# Revit family: QF_TRUE_TCGG-48-LD
name_source: partatom
category: Specialty Equipment
revit_build: Autodesk Revit 2014 (Build: 20130308_1515(x64)
units: mm (PartAtom-declared; Revit-internal decimal feet)

## types (1)
- DefaultType
    Apparent Power = 1357 VA
    Conn Conduit = Yes
    Conn Plug = 5-15P
    Cycle = 60 Hz
    Description = DISPLAY CASE: CURVED GLASS REFRIGERATED DELI CASE WITH LED LIGHTING
    FL Amps = 12 A
    HP = 1/3
    KCL SpecSheet URL = http://kclweb.kclcad.com
    KCLRef = KCL2C9,,0004091d-0000-0000-0000-000000000307,TF,TCGG-48 ,634854572620000000,716ea76f-1d88-4e94-8cc5-f22e7c59b278,a3fedd8f-e5fe-44fd-9469-5db82f1f6102
    Manufacturer = TRUE FOOD SERVICE EQUIPMENT, INC.
    Max Overcurrent Protection = 17 A
    Min Ckt Ampacity = 12 A
    Model = TCGG-48-LD
    Number of Poles = 1
    Phase = 1
    URL = www.truemfg.com
    URL Cutsheet = www.truemfg.com
    URL Manufacturer = www.truemfg.com
    Volts = 115 V
    Watts = 1357 W
    Weight in Pounds = 550

## geometry (parser evidence)
native form markers: Blend x16, Sweep x2
no freeform markers — native parametric forms only
